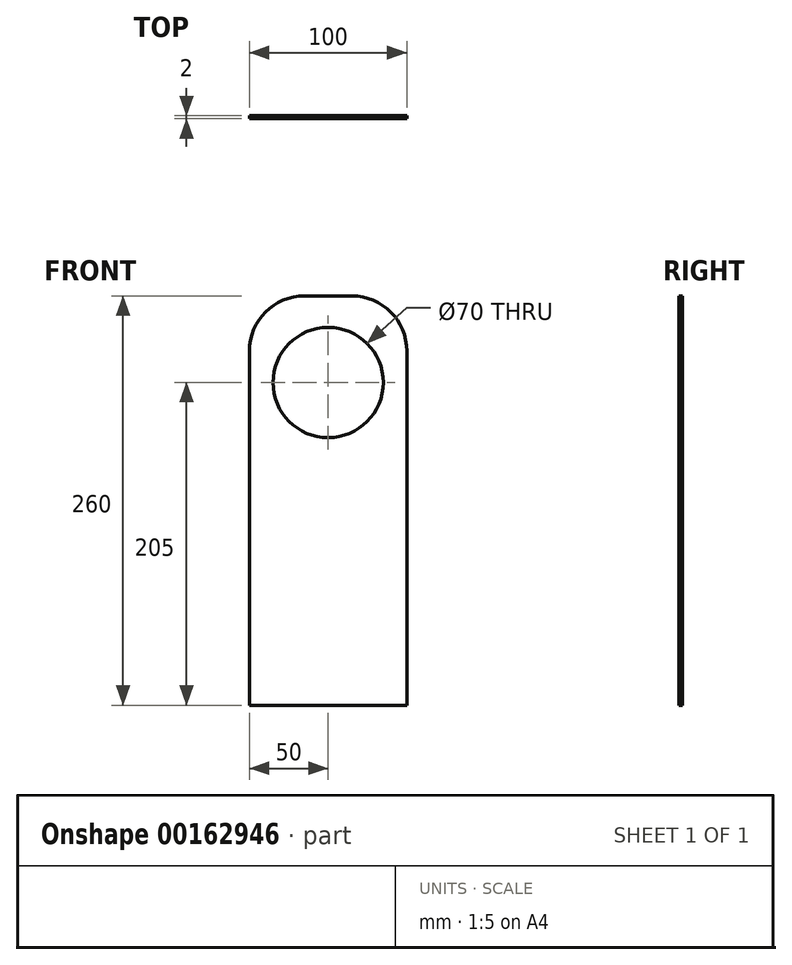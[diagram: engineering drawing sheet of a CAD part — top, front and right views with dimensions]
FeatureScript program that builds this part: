
annotation { "Feature Type Name" : "Feature", "Feature Type Description" : "" }
export const myFeature = defineFeature(function(context is Context, id is Id, definition is map)
    precondition{}
    {
        {
            var Q0;
            Q0=qCreatedBy(makeId("Front.planeOp"),FACE);
            var sketch = newSketch(context, id + "F0", { "sketchPlane" : qUnion([Q0])});
            skLineSegment(sketch, "E0.bottom", {"start": v(-15, 130) * mm, "end": v(15, 130) * mm});
            skLineSegment(sketch, "E0.top", {"start": v(-50, -130) * mm, "end": v(50, -130) * mm});
            skLineSegment(sketch, "E0.left", {"start": v(-50, 95) * mm, "end": v(-50, -130) * mm});
            skLineSegment(sketch, "E0.right", {"start": v(50, 95) * mm, "end": v(50, -130) * mm});
            skPoint(sketch, "E0.middle", {"position": v(0, 0) * mm});
            skCircle(sketch, "E1", {"center": v(0, 75) * mm, "radius": 35 * mm});
            skPoint(sketch, "E2.visualSharp", {"position": v(-50, 130) * mm});
            skArc(sketch, "E2.filletArc", {"start": v(-15, 130) * mm, "mid": v(-39.75, 119.75) * mm, "end": v(-50, 95) * mm});
            skPoint(sketch, "E3.visualSharp", {"position": v(50, 130) * mm});
            skArc(sketch, "E3.filletArc", {"start": v(50, 95) * mm, "mid": v(39.75, 119.75) * mm, "end": v(15, 130) * mm});
            skSolve(sketch);
        }
        {
            var Q0;
            Q0 = qSketchRegion(id + "F0", true);
            extrude(context, id + "F1", {"entities" : qUnion([Q0]), "depth" : 2 * mm});
        }
    });
